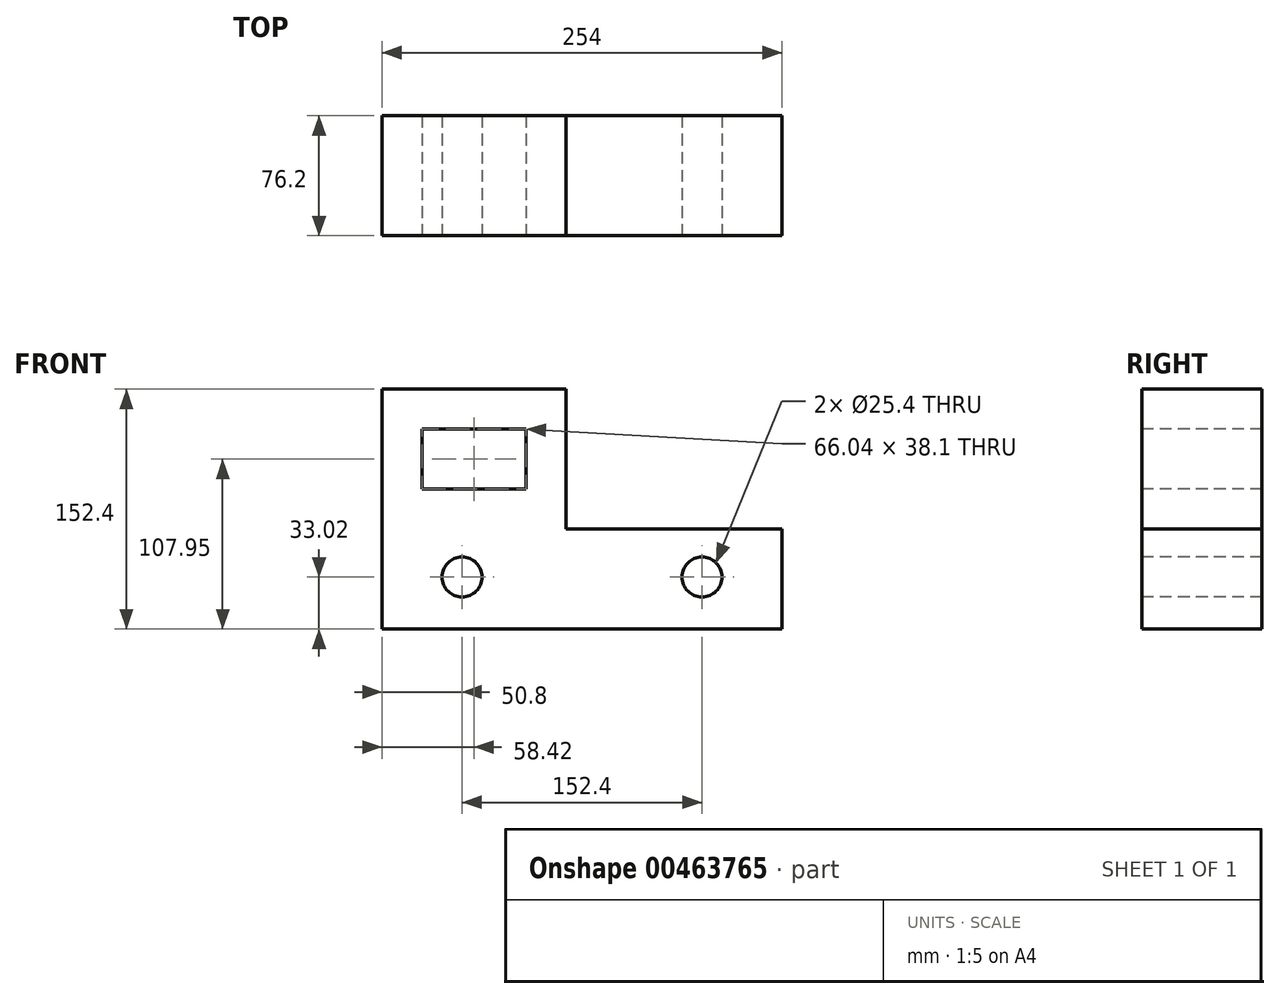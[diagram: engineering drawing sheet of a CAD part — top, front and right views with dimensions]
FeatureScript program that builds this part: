
annotation { "Feature Type Name" : "Feature", "Feature Type Description" : "" }
export const myFeature = defineFeature(function(context is Context, id is Id, definition is map)
    precondition{}
    {
        {
            var Q0;
            Q0=qCreatedBy(makeId("Front.planeOp"),FACE);
            var sketch = newSketch(context, id + "F0", { "sketchPlane" : qUnion([Q0])});
            skLineSegment(sketch, "E0", {"start": v(0, 152.4) * mm, "end": v(0, 0) * mm});
            skLineSegment(sketch, "E1", {"start": v(0, 0) * mm, "end": v(254, 0) * mm});
            skLineSegment(sketch, "E2", {"start": v(254, 0) * mm, "end": v(254, 63.5) * mm});
            skLineSegment(sketch, "E3", {"start": v(254, 63.5) * mm, "end": v(116.84, 63.5) * mm});
            skLineSegment(sketch, "E4", {"start": v(116.84, 63.5) * mm, "end": v(116.84, 152.4) * mm});
            skLineSegment(sketch, "E5", {"start": v(116.84, 152.4) * mm, "end": v(0, 152.4) * mm});
            skSolve(sketch);
        }
        {
            var Q0;
            Q0=makeQuery(id+"F0.imprint","IMPRINT",FACE,{"disambiguationData":[TD([[makeQuery(id+"F0.imprint","IMPRINT",EDGE,{"derivedFrom":sQuery(id+"F0.wireOp",EDGE,"E0")}),1.0]])]});
            extrude(context, id + "F1", {"entities" : qUnion([Q0]), "depth" : 76.2 * mm});
        }
        {
            var Q0;
            Q0=makeQuery(id+"F1.opExtrude","CAP_FACE",FACE,{"disambiguationData":[OSD([sQuery(id+"F0.wireOp",EDGE,"E0"),sQuery(id+"F0.wireOp",EDGE,"E1"),sQuery(id+"F0.wireOp",EDGE,"E2"),sQuery(id+"F0.wireOp",EDGE,"E3"),sQuery(id+"F0.wireOp",EDGE,"E4"),sQuery(id+"F0.wireOp",EDGE,"E5")])],"isStart":false});
            var sketch = newSketch(context, id + "F2", { "sketchPlane" : qUnion([Q0])});
            skLineSegment(sketch, "E6.bottom", {"start": v(25.4, 127) * mm, "end": v(91.44, 127) * mm});
            skLineSegment(sketch, "E6.top", {"start": v(25.4, 88.9) * mm, "end": v(91.44, 88.9) * mm});
            skLineSegment(sketch, "E6.left", {"start": v(25.4, 127) * mm, "end": v(25.4, 88.9) * mm});
            skLineSegment(sketch, "E6.right", {"start": v(91.44, 127) * mm, "end": v(91.44, 88.9) * mm});
            skSolve(sketch);
        }
        {
            var Q0;
            Q0=makeQuery(id+"F2.imprint","IMPRINT",FACE,{"disambiguationData":[TD([[makeQuery(id+"F2.imprint","IMPRINT",EDGE,{"derivedFrom":sQuery(id+"F2.wireOp",EDGE,"E6.bottom")}),-1.0]])]});
            extrude(context, id + "F3", {"entities" : qUnion([Q0]), "operationType" : NewBodyOperationType.REMOVE, "oppositeDirection" : true, "depth" : 787.4 * mm});
        }
        {
            var Q0;
            Q0=makeQuery(id+"F1.opExtrude","CAP_FACE",FACE,{"disambiguationData":[OSD([sQuery(id+"F0.wireOp",EDGE,"E0"),sQuery(id+"F0.wireOp",EDGE,"E1"),sQuery(id+"F0.wireOp",EDGE,"E2"),sQuery(id+"F0.wireOp",EDGE,"E3"),sQuery(id+"F0.wireOp",EDGE,"E4"),sQuery(id+"F0.wireOp",EDGE,"E5")])],"isStart":false});
            var sketch = newSketch(context, id + "F4", { "sketchPlane" : qUnion([Q0])});
            skCircle(sketch, "E7", {"center": v(50.8, 33.02) * mm, "radius": 12.7 * mm});
            skCircle(sketch, "E8", {"center": v(203.2, 33.02) * mm, "radius": 12.7 * mm});
            skSolve(sketch);
        }
        {
            var Q0;
            Q0=makeQuery(id+"F4.imprint","IMPRINT",FACE,{"disambiguationData":[TD([[makeQuery(id+"F4.imprint","IMPRINT",EDGE,{"derivedFrom":sQuery(id+"F4.wireOp",EDGE,"E7")}),1.0]])]});
            var Q1;
            Q1=makeQuery(id+"F4.imprint","IMPRINT",FACE,{"disambiguationData":[TD([[makeQuery(id+"F4.imprint","IMPRINT",EDGE,{"derivedFrom":sQuery(id+"F4.wireOp",EDGE,"E8")}),1.0]])]});
            extrude(context, id + "F5", {"entities" : qUnion([Q0, Q1]), "operationType" : NewBodyOperationType.REMOVE, "oppositeDirection" : true, "depth" : 78.74 * mm});
        }
    });
